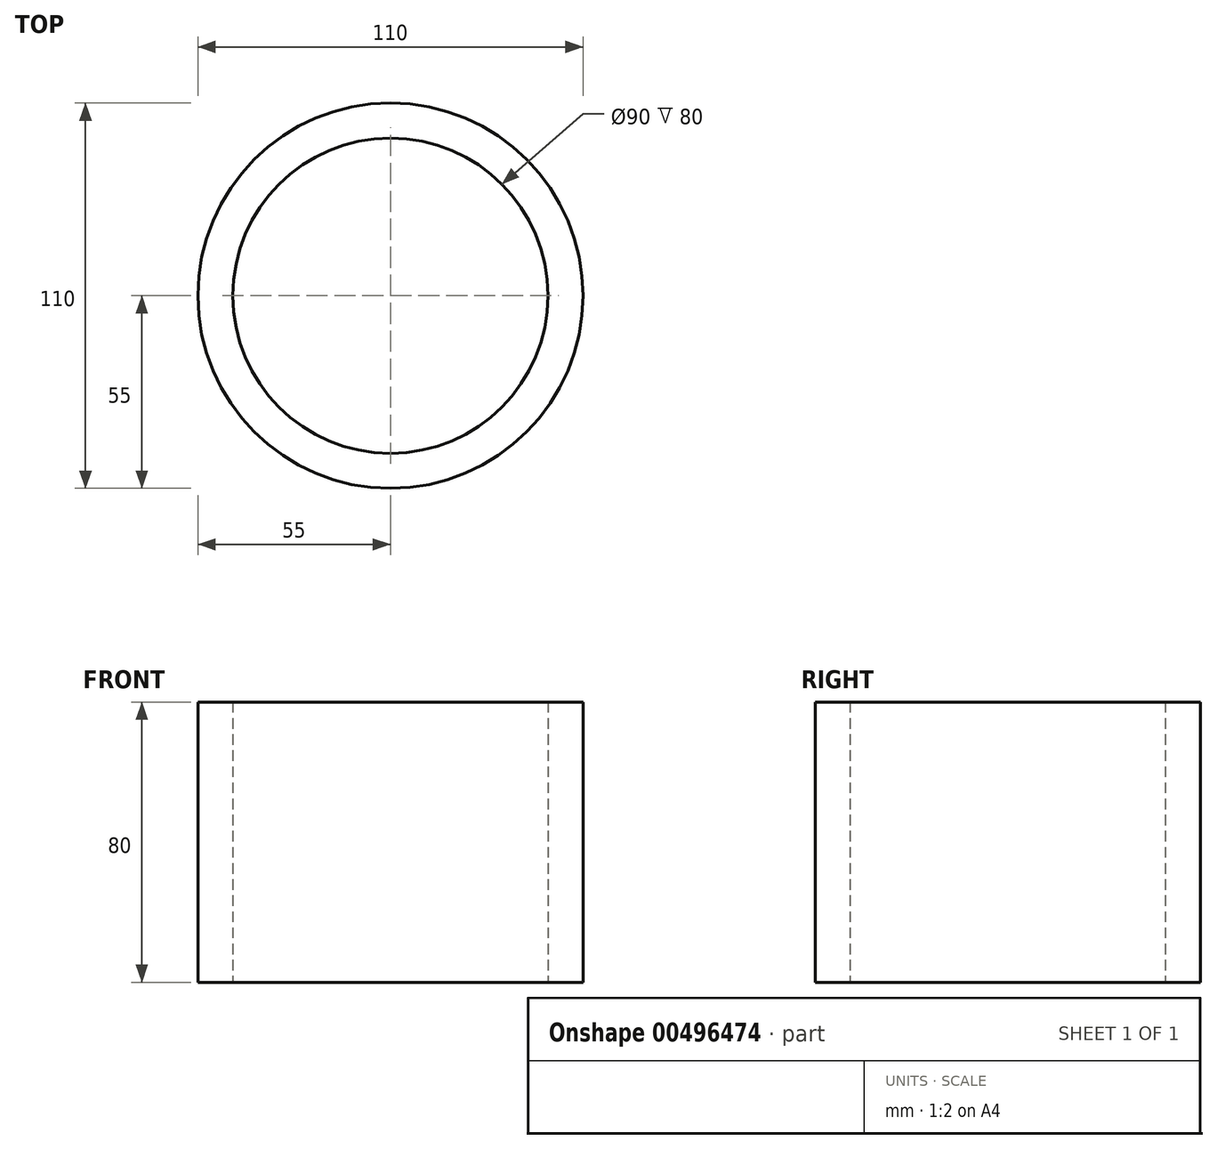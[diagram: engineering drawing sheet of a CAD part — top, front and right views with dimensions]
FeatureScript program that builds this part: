
annotation { "Feature Type Name" : "Feature", "Feature Type Description" : "" }
export const myFeature = defineFeature(function(context is Context, id is Id, definition is map)
    precondition{}
    {
        {
            var Q0;
            Q0=qCreatedBy(makeId("Top.planeOp"),FACE);
            var sketch = newSketch(context, id + "F0", { "sketchPlane" : qUnion([Q0])});
            skCircle(sketch, "E0", {"center": v(0, 0) * mm, "radius": 45 * mm});
            skCircle(sketch, "E1", {"center": v(0, 0) * mm, "radius": 55 * mm});
            skSolve(sketch);
        }
        {
            var Q0;
            Q0=makeQuery(id+"F0.imprint","IMPRINT",FACE,{"disambiguationData":[TD([[makeQuery(id+"F0.imprint","IMPRINT",EDGE,{"derivedFrom":sQuery(id+"F0.wireOp",EDGE,"E0")}),-1.0]])]});
            extrude(context, id + "F1", {"entities" : qUnion([Q0]), "depth" : 80 * mm});
        }
    });
